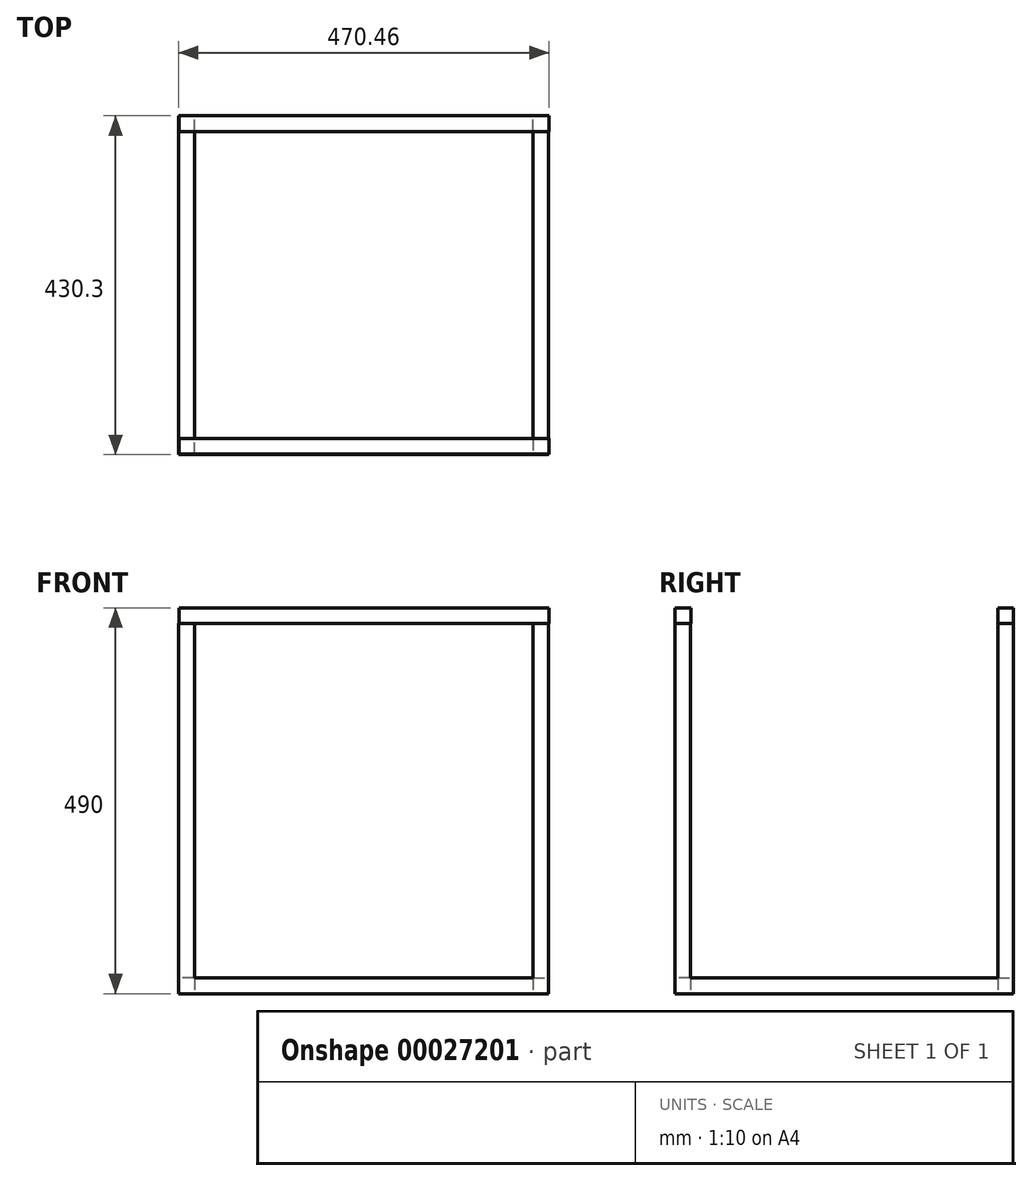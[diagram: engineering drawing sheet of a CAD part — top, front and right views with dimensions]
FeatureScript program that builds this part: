
annotation { "Feature Type Name" : "Feature", "Feature Type Description" : "" }
export const myFeature = defineFeature(function(context is Context, id is Id, definition is map)
    precondition{}
    {
        {
            var Q0;
            Q0=qCreatedBy(makeId("Top.planeOp"),FACE);
            var sketch = newSketch(context, id + "F0", { "sketchPlane" : qUnion([Q0])});
            skLineSegment(sketch, "E0.rect.bottom", {"start": v(235, 10) * mm, "end": v(-235, 10) * mm});
            skLineSegment(sketch, "E0.rect.top", {"start": v(235, -10) * mm, "end": v(-235, -10) * mm});
            skLineSegment(sketch, "E0.rect.left", {"start": v(235, 10) * mm, "end": v(235, -10) * mm});
            skLineSegment(sketch, "E0.rect.right", {"start": v(-235, 10) * mm, "end": v(-235, -10) * mm});
            skPoint(sketch, "E0.rect.middle", {"position": v(0, 0) * mm});
            skLineSegment(sketch, "E1.bottom", {"start": v(-235, 10) * mm, "end": v(-215, 10) * mm});
            skLineSegment(sketch, "E1.top", {"start": v(-235, 400) * mm, "end": v(-215, 400) * mm});
            skLineSegment(sketch, "E1.left", {"start": v(-235, 10) * mm, "end": v(-235, 400) * mm});
            skLineSegment(sketch, "E1.right", {"start": v(-215, 10) * mm, "end": v(-215, 400) * mm});
            skLineSegment(sketch, "E2.bottom", {"start": v(235, 10) * mm, "end": v(215, 10) * mm});
            skLineSegment(sketch, "E2.top", {"start": v(235, 400) * mm, "end": v(215, 400) * mm});
            skLineSegment(sketch, "E2.left", {"start": v(235, 10) * mm, "end": v(235, 400) * mm});
            skLineSegment(sketch, "E2.right", {"start": v(215, 10) * mm, "end": v(215, 400) * mm});
            skLineSegment(sketch, "E3.bottom", {"start": v(235, 400) * mm, "end": v(-235.06, 400) * mm});
            skLineSegment(sketch, "E3.top", {"start": v(235, 420) * mm, "end": v(-235.06, 420) * mm});
            skLineSegment(sketch, "E3.left", {"start": v(235, 400) * mm, "end": v(235, 420) * mm});
            skLineSegment(sketch, "E3.right", {"start": v(-235.06, 400) * mm, "end": v(-235.06, 420) * mm});
            skSolve(sketch);
        }
        {
            var Q0;
            Q0=qSketchRegion(id+"F0",true);
            extrude(context, id + "F1", {"entities" : qUnion([Q0]), "depth" : 20 * mm});
        }
        {
            var Q0;
            Q0=makeQuery(id+"F1.opExtrude","CAP_FACE",FACE,{"disambiguationData":[OSD([sQuery(id+"F0.wireOp",EDGE,"E0.rect.bottom"),sQuery(id+"F0.wireOp",EDGE,"E0.rect.top"),sQuery(id+"F0.wireOp",EDGE,"E0.rect.left"),sQuery(id+"F0.wireOp",EDGE,"E0.rect.right"),sQuery(id+"F0.wireOp",EDGE,"E1.left"),sQuery(id+"F0.wireOp",EDGE,"E1.right"),sQuery(id+"F0.wireOp",EDGE,"E2.left"),sQuery(id+"F0.wireOp",EDGE,"E2.right"),sQuery(id+"F0.wireOp",EDGE,"E3.bottom"),sQuery(id+"F0.wireOp",EDGE,"E3.top"),sQuery(id+"F0.wireOp",EDGE,"E3.left"),sQuery(id+"F0.wireOp",EDGE,"E3.right")])],"isStart":false});
            var sketch = newSketch(context, id + "F2", { "sketchPlane" : qUnion([Q0])});
            skLineSegment(sketch, "E4.bottom", {"start": v(-235, -10) * mm, "end": v(-215, -10) * mm});
            skLineSegment(sketch, "E4.top", {"start": v(-235, 10) * mm, "end": v(-215, 10) * mm});
            skLineSegment(sketch, "E4.left", {"start": v(-235, -10) * mm, "end": v(-235, 10) * mm});
            skLineSegment(sketch, "E4.right", {"start": v(-215, -10) * mm, "end": v(-215, 10) * mm});
            skLineSegment(sketch, "E5.bottom", {"start": v(215, 10) * mm, "end": v(235, 10) * mm});
            skLineSegment(sketch, "E5.top", {"start": v(215, -10) * mm, "end": v(235, -10) * mm});
            skLineSegment(sketch, "E5.left", {"start": v(215, 10) * mm, "end": v(215, -10) * mm});
            skLineSegment(sketch, "E5.right", {"start": v(235, 10) * mm, "end": v(235, -10) * mm});
            skLineSegment(sketch, "E6.bottom", {"start": v(-215, 400) * mm, "end": v(-235.06, 400) * mm});
            skLineSegment(sketch, "E6.top", {"start": v(-215, 420) * mm, "end": v(-235.06, 420) * mm});
            skLineSegment(sketch, "E6.left", {"start": v(-215, 400) * mm, "end": v(-215, 420) * mm});
            skLineSegment(sketch, "E6.right", {"start": v(-235.06, 400) * mm, "end": v(-235.06, 420) * mm});
            skLineSegment(sketch, "E7.bottom", {"start": v(215, 400) * mm, "end": v(235, 400) * mm});
            skLineSegment(sketch, "E7.top", {"start": v(215, 420) * mm, "end": v(235, 420) * mm});
            skLineSegment(sketch, "E7.left", {"start": v(215, 400) * mm, "end": v(215, 420) * mm});
            skLineSegment(sketch, "E7.right", {"start": v(235, 400) * mm, "end": v(235, 420) * mm});
            skSolve(sketch);
        }
        {
            var Q0;
            Q0=qSketchRegion(id+"F2",true);
            extrude(context, id + "F3", {"entities" : qUnion([Q0]), "operationType" : NewBodyOperationType.ADD, "depth" : 450 * mm});
        }
        {
            var Q0;
            Q0=makeQuery(id+"F3.opExtrude","CAP_FACE",FACE,{"disambiguationData":[OSD([sQuery(id+"F2.wireOp",EDGE,"E4.bottom"),sQuery(id+"F2.wireOp",EDGE,"E4.top"),sQuery(id+"F2.wireOp",EDGE,"E4.left"),sQuery(id+"F2.wireOp",EDGE,"E4.right")])],"isStart":false});
            var sketch = newSketch(context, id + "F4", { "sketchPlane" : qUnion([Q0])});
            skLineSegment(sketch, "E8.rect.bottom", {"start": v(235.4, 10.3) * mm, "end": v(-234.6, 10.3) * mm});
            skLineSegment(sketch, "E8.rect.top", {"start": v(235.4, -9.7) * mm, "end": v(-234.6, -9.7) * mm});
            skLineSegment(sketch, "E8.rect.left", {"start": v(235.4, 10.3) * mm, "end": v(235.4, -9.7) * mm});
            skLineSegment(sketch, "E8.rect.right", {"start": v(-234.6, 10.3) * mm, "end": v(-234.6, -9.7) * mm});
            skPoint(sketch, "E8.rect.middle", {"position": v(0.4, 0.3) * mm});
            skLineSegment(sketch, "E9.bottom", {"start": v(-234.6, 10.3) * mm, "end": v(-214.6, 10.3) * mm});
            skLineSegment(sketch, "E9.top", {"start": v(-234.6, 400.3) * mm, "end": v(-214.6, 400.3) * mm});
            skLineSegment(sketch, "E9.left", {"start": v(-234.6, 10.3) * mm, "end": v(-234.6, 400.3) * mm});
            skLineSegment(sketch, "E9.right", {"start": v(-214.6, 10.3) * mm, "end": v(-214.6, 400.3) * mm});
            skLineSegment(sketch, "E10.bottom", {"start": v(235.4, 10.3) * mm, "end": v(215.4, 10.3) * mm});
            skLineSegment(sketch, "E10.top", {"start": v(235.4, 400.3) * mm, "end": v(215.4, 400.3) * mm});
            skLineSegment(sketch, "E10.left", {"start": v(235.4, 10.3) * mm, "end": v(235.4, 400.3) * mm});
            skLineSegment(sketch, "E10.right", {"start": v(215.4, 10.3) * mm, "end": v(215.4, 400.3) * mm});
            skLineSegment(sketch, "E11.bottom", {"start": v(235.4, 400.3) * mm, "end": v(-234.67, 400.3) * mm});
            skLineSegment(sketch, "E11.top", {"start": v(235.4, 420.3) * mm, "end": v(-234.67, 420.3) * mm});
            skLineSegment(sketch, "E11.left", {"start": v(235.4, 400.3) * mm, "end": v(235.4, 420.3) * mm});
            skLineSegment(sketch, "E11.right", {"start": v(-234.67, 400.3) * mm, "end": v(-234.67, 420.3) * mm});
            skSolve(sketch);
        }
        {
            var Q0;
            Q0=makeQuery(id+"F4.imprint","IMPRINT",FACE,{"disambiguationData":[TD([[makeQuery(id+"F4.imprint","IMPRINT",EDGE,{"derivedFrom":sQuery(id+"F4.wireOp",EDGE,"E8.rect.bottom")}),1.0]])]});
            var Q1;
            Q1=makeQuery(id+"F4.imprint","IMPRINT",FACE,{"disambiguationData":[TD([[makeQuery(id+"F4.imprint","IMPRINT",EDGE,{"derivedFrom":sQuery(id+"F4.wireOp",EDGE,"E10.bottom")}),-1.0]])]});
            var Q2;
            Q2=makeQuery(id+"F4.imprint","IMPRINT",FACE,{"disambiguationData":[TD([[makeQuery(id+"F4.imprint","IMPRINT",EDGE,{"derivedFrom":sQuery(id+"F4.wireOp",EDGE,"E11.top")}),1.0]])]});
            var Q3;
            Q3=makeQuery(id+"F4.imprint","IMPRINT",FACE,{"disambiguationData":[TD([[makeQuery(id+"F4.imprint","IMPRINT",EDGE,{"derivedFrom":sQuery(id+"F4.wireOp",EDGE,"E9.bottom")}),1.0]])]});
            var Q4;
            {var subQ1=sQuery(id+"F4.wireOp",EDGE,"E8.rect.top");var subQ5=sQuery(id+"F4.wireOp",EDGE,"E8.rect.right");var subQ7=makeQuery(id+"F4.imprint","INTERSECT",VERTEX,{"derivedFrom":[subQ1,subQ5]});Q4=makeQuery(id+"F4.imprint","IMPRINT",FACE,{"disambiguationData":[TD([[makeQuery(id+"F4.imprint","IMPRINT",EDGE,{"disambiguationData":[TD([[subQ7,1.0]])],"derivedFrom":subQ1}),-1.0]])]});}
            extrude(context, id + "F5", {"entities" : qUnion([Q0, Q1, Q2, Q3, Q4]), "operationType" : NewBodyOperationType.ADD, "depth" : 20 * mm});
        }
    });
